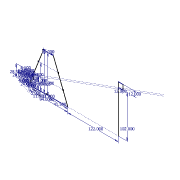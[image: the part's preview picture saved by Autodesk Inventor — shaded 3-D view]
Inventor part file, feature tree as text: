
AUTODESK INVENTOR PART (.ipt)
format: ipt  version: 2012 (Build 160160000, 160)  size: 111,616 bytes
history: native  units: in
note: dims shown in document units (in); Inventor stores cm internally (conversion verified against a paired STEP export)
features: sketch x1
ambient origin geometry x8: Origin, YZ Plane, XZ Plane, XY Plane, X Axis, Y Axis, Z Axis, Center Point
feature tree (1):
  sketch  "Sketch1"  dims[d0=4.0in d1=24.0in d2=11.0in d8=11.0in d16=3.0in d28=28.5in d33=20.0in d35=3.0in d36=20.0in d37=8.5in d40=9.0in d42=11.0in d43=1.0in d44=0.1374in d45=24.0in d46=90.0in d47=94.0in d48=1.5in d49=90.0in d50=60.0in d51=30.0in d52=12.0in d53=102.0in d54=122.0in d55=12.0in d56=11.0in d57=41.5in d58=5.5in d59=8.0in d60=5.0in d61=9.5in d62=0.7559in d63=0.7559in d68=2.0in d69=6.0in d70=5.5in d71=12.0in]
